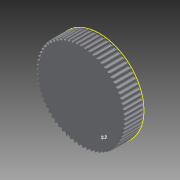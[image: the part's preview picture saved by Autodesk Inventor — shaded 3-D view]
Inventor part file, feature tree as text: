
AUTODESK INVENTOR PART (.ipt)
format: ipt  version: 2015 SP1 (Build 190203100, 203)  size: 439,808 bytes
history: native  units: in
note: dims shown in document units (in); Inventor stores cm internally (conversion verified against a paired STEP export)
features: other x3, extrude x2, pattern_circular x1, imported_body x1, projected_geometry x1
ambient origin geometry x8: Origin, YZ Plane, XZ Plane, XY Plane, X Axis, Y Axis, Z Axis, Center Point
bodies: Solid1 (feature_tree)
feature tree (8):
  other  "HTD3-66T stock a_6a22m066tm201"
  other  "Projected66TProfile"
  other  "ProfileModifiedForPrinter"
  extrude  "Base"  TaperAngle=0.0deg  [1 undecoded]
  extrude  "Extrusion4"  Depth=0.3937in TaperAngle=0.0deg
  pattern_circular  "Circular Pattern2"  Count=66 Angle=360.0deg
  imported_body  "Base1"
  projected_geometry  "Projected Loop1"
note: 1 required parameter value undecoded (feature->parameter linkage not recoverable at this tier; creation-order binding heuristic only, values carry confidence <= 0.55)
